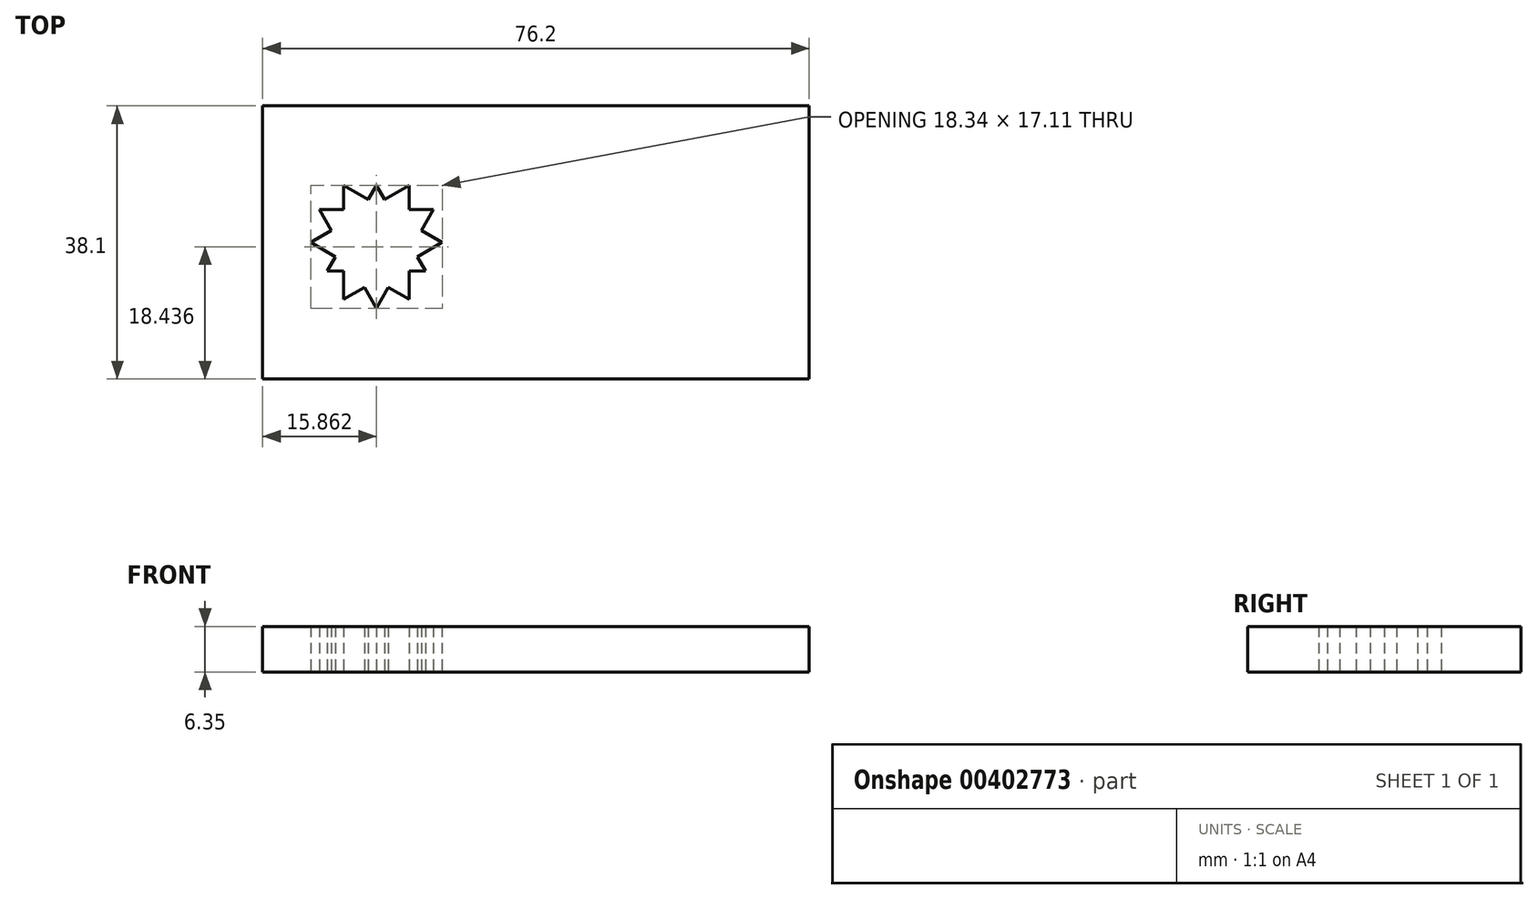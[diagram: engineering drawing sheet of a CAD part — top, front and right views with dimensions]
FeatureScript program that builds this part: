
annotation { "Feature Type Name" : "Feature", "Feature Type Description" : "" }
export const myFeature = defineFeature(function(context is Context, id is Id, definition is map)
    precondition{}
    {
        {
            var Q0;
            Q0=qCreatedBy(makeId("Top.planeOp"),FACE);
            var sketch = newSketch(context, id + "F0", { "sketchPlane" : qUnion([Q0])});
            skLineSegment(sketch, "E0.bottom", {"start": v(-38.1, 19.05) * mm, "end": v(38.1, 19.05) * mm});
            skLineSegment(sketch, "E0.top", {"start": v(-38.1, -19.05) * mm, "end": v(38.1, -19.05) * mm});
            skLineSegment(sketch, "E0.left", {"start": v(-38.1, 19.05) * mm, "end": v(-38.1, -19.05) * mm});
            skLineSegment(sketch, "E0.right", {"start": v(38.1, 19.05) * mm, "end": v(38.1, -19.05) * mm});
            skPoint(sketch, "E0.middle", {"position": v(0, 0) * mm});
            skCircle(sketch, "E1.cCircle", {"center": v(-22.24, 0) * mm, "radius": 4.59 * mm, "construction": true});
            skLineSegment(sketch, "E1.0", {"start": v(-17.65, 7.94) * mm, "end": v(-17.65, -7.94) * mm});
            skLineSegment(sketch, "E1.1", {"start": v(-17.65, -7.94) * mm, "end": v(-31.4, 0) * mm});
            skLineSegment(sketch, "E1.2", {"start": v(-31.4, 0) * mm, "end": v(-17.65, 7.94) * mm});
            skPoint(sketch, "E1.0.midPoint", {"position": v(-17.65, 0) * mm});
            skLineSegment(sketch, "E2.0", {"start": v(-26.82, -7.94) * mm, "end": v(-26.82, 7.94) * mm});
            skLineSegment(sketch, "E2.1", {"start": v(-26.82, 7.94) * mm, "end": v(-13.07, 0) * mm});
            skLineSegment(sketch, "E2.2", {"start": v(-13.07, 0) * mm, "end": v(-26.82, -7.94) * mm});
            skPoint(sketch, "E2.0.midPoint", {"position": v(-26.82, 0) * mm});
            skCircle(sketch, "E3.cCircle", {"center": v(-22.24, 0) * mm, "radius": 3.97 * mm, "construction": true});
            skPoint(sketch, "E3.cCircle.perimeterSnap0", {"position": v(-24.53, -3.97) * mm});
            skLineSegment(sketch, "E3.0", {"start": v(-15.36, -3.97) * mm, "end": v(-29.12, -3.97) * mm});
            skLineSegment(sketch, "E3.1", {"start": v(-29.12, -3.97) * mm, "end": v(-22.24, 7.94) * mm});
            skLineSegment(sketch, "E3.2", {"start": v(-22.24, 7.94) * mm, "end": v(-15.36, -3.97) * mm});
            skPoint(sketch, "E3.0.midPoint", {"position": v(-22.24, -3.97) * mm});
            skPoint(sketch, "E3.0.midPoint.positionSnap0", {"position": v(-24.53, -3.97) * mm});
            skLineSegment(sketch, "E4.0", {"start": v(-30.18, 4.59) * mm, "end": v(-14.3, 4.59) * mm});
            skLineSegment(sketch, "E4.1", {"start": v(-14.3, 4.59) * mm, "end": v(-22.24, -9.17) * mm});
            skLineSegment(sketch, "E4.2", {"start": v(-22.24, -9.17) * mm, "end": v(-30.18, 4.59) * mm});
            skPoint(sketch, "E4.0.midPoint", {"position": v(-22.24, 4.59) * mm});
            skSolve(sketch);
        }
        {
            var Q0;
            Q0=makeQuery(id+"F0.imprint","IMPRINT",FACE,{"disambiguationData":[TD([[makeQuery(id+"F0.imprint","IMPRINT",EDGE,{"derivedFrom":sQuery(id+"F0.wireOp",EDGE,"E0.bottom")}),-1.0]])]});
            extrude(context, id + "F1", {"entities" : qUnion([Q0]), "depth" : 6.35 * mm});
        }
    });
